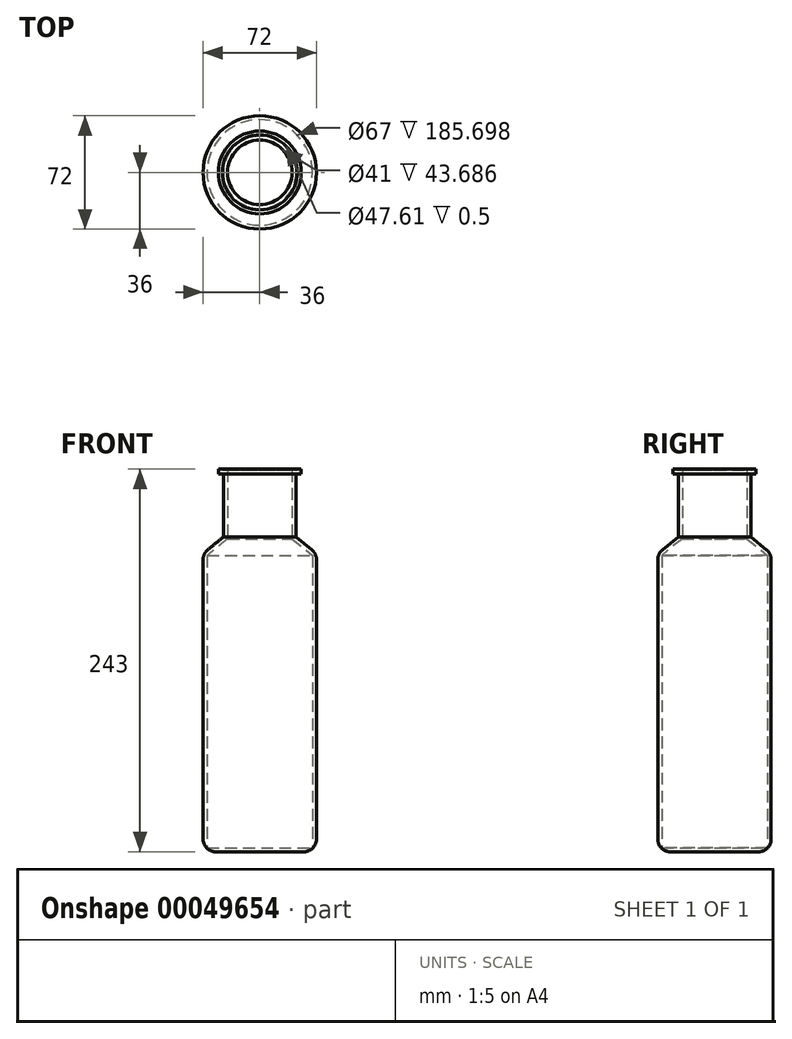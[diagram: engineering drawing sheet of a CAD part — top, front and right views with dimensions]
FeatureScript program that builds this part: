
annotation { "Feature Type Name" : "Feature", "Feature Type Description" : "" }
export const myFeature = defineFeature(function(context is Context, id is Id, definition is map)
    precondition{}
    {
        {
            var Q0;
            Q0=qCreatedBy(makeId("Front.planeOp"),FACE);
            var sketch = newSketch(context, id + "F0", { "sketchPlane" : qUnion([Q0])});
            skLineSegment(sketch, "E0", {"start": v(0, 0) * mm, "end": v(36, 0) * mm});
            skLineSegment(sketch, "E1", {"start": v(36, 0) * mm, "end": v(36, 189.38) * mm});
            skLineSegment(sketch, "E2", {"start": v(36, 189.38) * mm, "end": v(23, 200) * mm});
            skLineSegment(sketch, "E3", {"start": v(23, 200) * mm, "end": v(23, 240) * mm});
            skLineSegment(sketch, "E4", {"start": v(23, 240) * mm, "end": v(26.3, 240) * mm});
            skLineSegment(sketch, "E5", {"start": v(26.3, 240) * mm, "end": v(26.3, 243) * mm});
            skLineSegment(sketch, "E6", {"start": v(26.3, 243) * mm, "end": v(0, 243) * mm});
            skLineSegment(sketch, "E7", {"start": v(0, 0) * mm, "end": v(0, 243) * mm});
            skSolve(sketch);
        }
        {
            var Q0;
            Q0=makeQuery(id+"F0.imprint","IMPRINT",FACE,{"disambiguationData":[TD([[makeQuery(id+"F0.imprint","IMPRINT",EDGE,{"derivedFrom":sQuery(id+"F0.wireOp",EDGE,"E0")}),1.0]])]});
            var Q1;
            Q1=sQuery(id+"F0.wireOp",EDGE,"E7");
            revolve(context, id + "F1", {"entities" : qUnion([Q0]), "axis" : qUnion([Q1]), "revolveType" : RevolveType.FULL});
        }
        {
            var Q0;
            Q0=makeQuery(id+"F1.opRevolve","SWEPT_FACE",FACE,{"disambiguationData":[OSD([sQuery(id+"F0.wireOp",EDGE,"E6")])]});
            shell(context, id + "F2", {"entities" : qUnion([Q0]), "thickness" : 2.5 * mm});
        }
        {
            var Q0;
            Q0=makeQuery(id+"F1.opRevolve","SWEPT_EDGE",EDGE,{"disambiguationData":[OSD([sQuery(id+"F0.wireOp",EDGE,"E0"),sQuery(id+"F0.wireOp",EDGE,"E1")])]});
            var Q1;
            Q1=makeQuery(id+"F1.opRevolve","SWEPT_EDGE",EDGE,{"disambiguationData":[OSD([sQuery(id+"F0.wireOp",EDGE,"E1"),sQuery(id+"F0.wireOp",EDGE,"E2")])]});
            fillet(context, id + "F3", {"entities" : qUnion([Q0, Q1]), "radius" : 8 * mm, "tangentPropagation" : true, "allowEdgeOverflow" : false});
        }
    });
